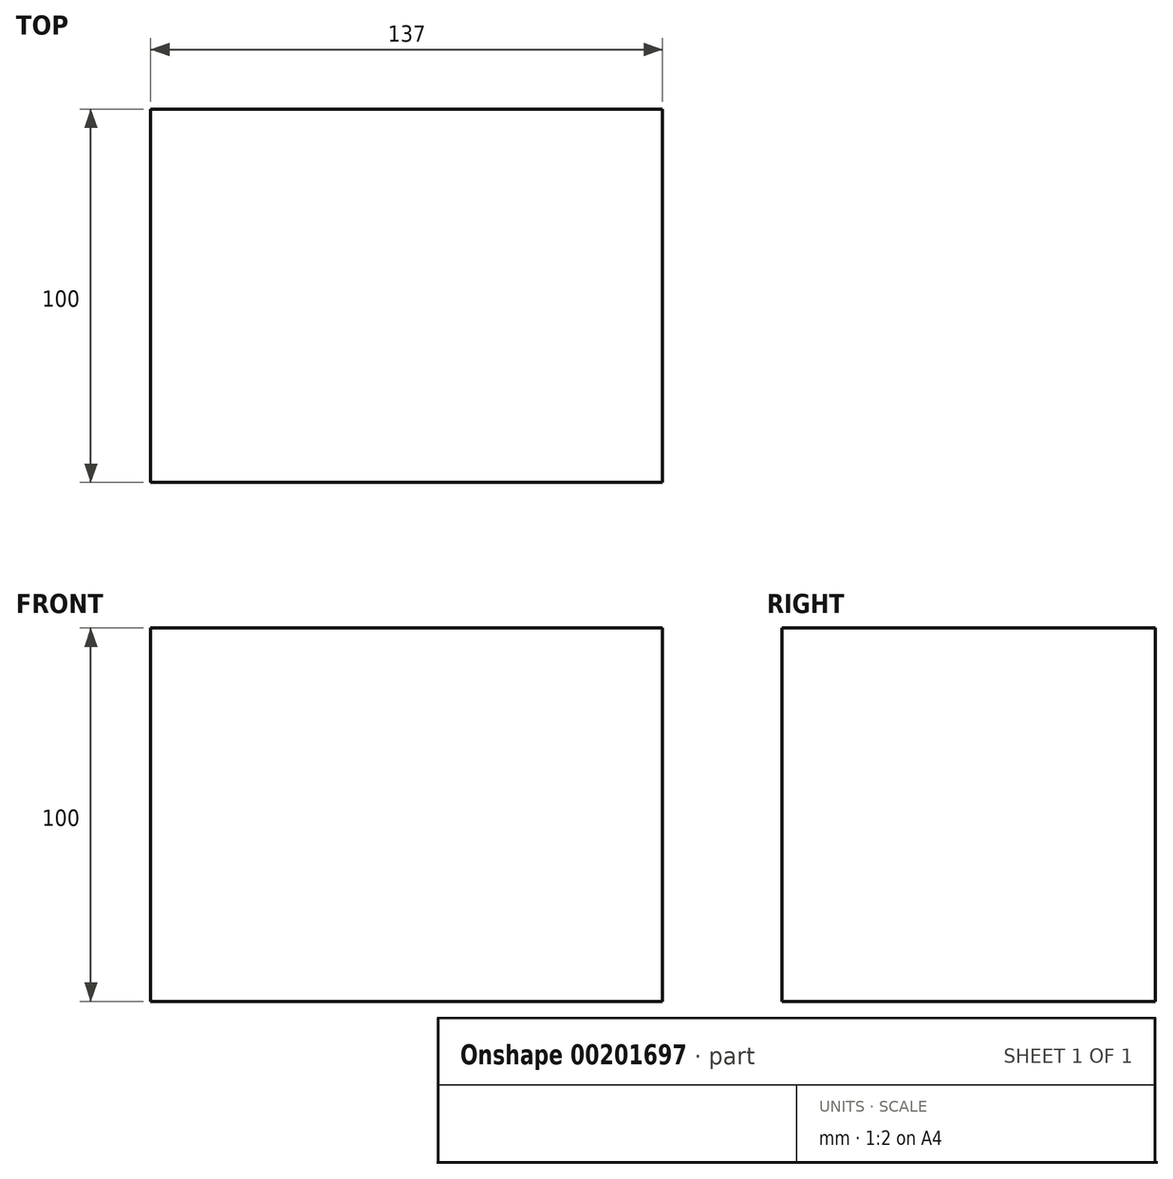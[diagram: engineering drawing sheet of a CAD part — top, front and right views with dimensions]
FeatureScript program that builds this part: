
annotation { "Feature Type Name" : "Feature", "Feature Type Description" : "" }
export const myFeature = defineFeature(function(context is Context, id is Id, definition is map)
    precondition{}
    {
        {
            var Q0;
            Q0=qCreatedBy(makeId("Right.planeOp"),FACE);
            var sketch = newSketch(context, id + "F0", { "sketchPlane" : qUnion([Q0])});
            skLineSegment(sketch, "E0", {"start": v(0, 0) * mm, "end": v(100, 0) * mm});
            skLineSegment(sketch, "E1", {"start": v(100, 0) * mm, "end": v(100, 100) * mm});
            skLineSegment(sketch, "E2", {"start": v(100, 100) * mm, "end": v(0, 100) * mm});
            skLineSegment(sketch, "E3", {"start": v(0, 100) * mm, "end": v(0, 0) * mm});
            skLineSegment(sketch, "E4", {"start": v(50, 100) * mm, "end": v(50, 55) * mm});
            skLineSegment(sketch, "E5", {"start": v(50, 55) * mm, "end": v(100, 55) * mm});
            skArc(sketch, "E6", {"start": v(63.75, 0) * mm, "mid": v(50, 13.75) * mm, "end": v(36.25, 0) * mm});
            skSolve(sketch);
        }
        {
            var Q0;
            Q0 = qSketchRegion(id + "F0", true);
            extrude(context, id + "F1", {"entities" : qUnion([Q0]), "oppositeDirection" : true, "depth" : 137 * mm});
        }
    });
